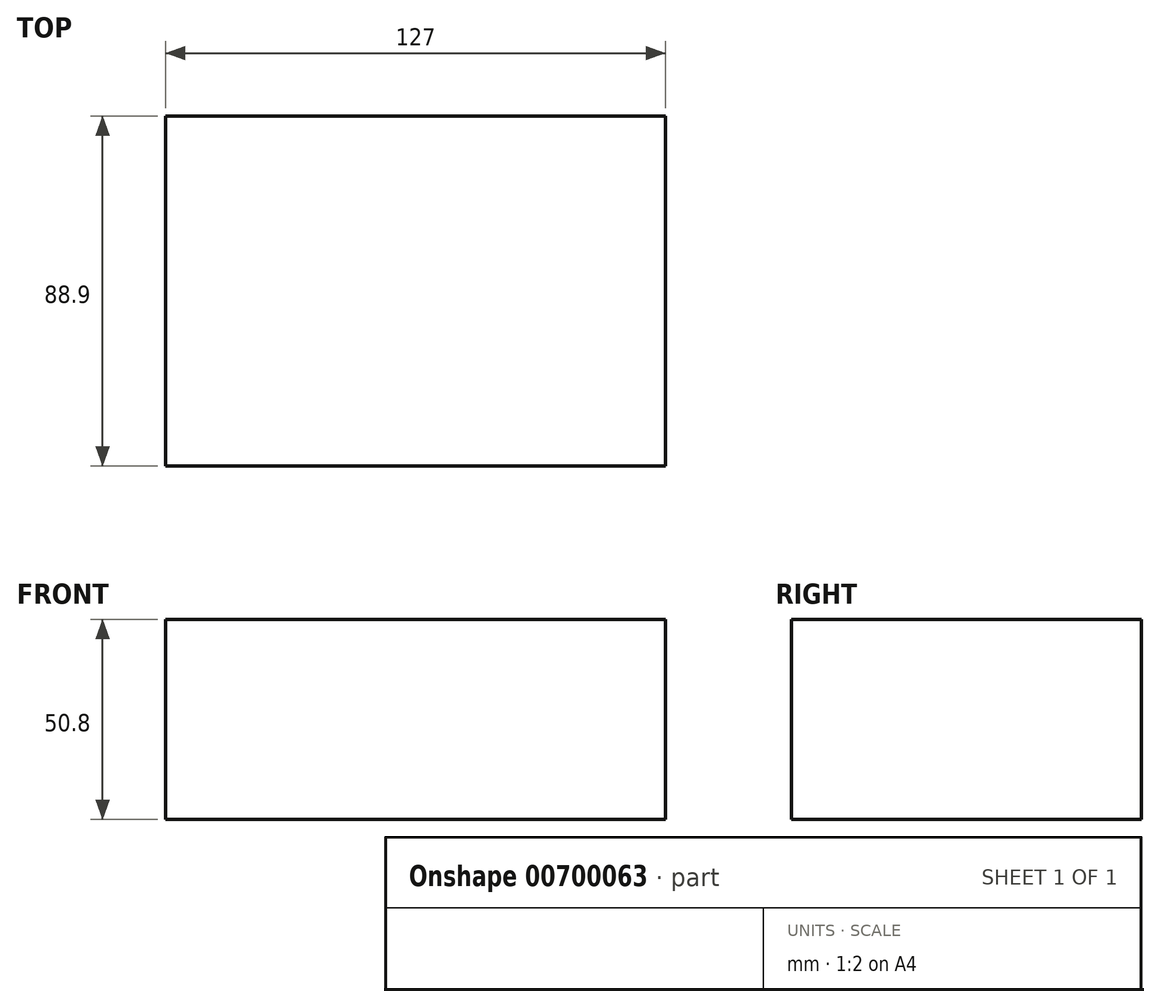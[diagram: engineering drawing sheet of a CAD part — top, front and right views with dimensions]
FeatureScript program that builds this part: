
annotation { "Feature Type Name" : "Feature", "Feature Type Description" : "" }
export const myFeature = defineFeature(function(context is Context, id is Id, definition is map)
    precondition{}
    {
        {
            var Q0;
            Q0=qCreatedBy(makeId("Front.planeOp"),FACE);
            var sketch = newSketch(context, id + "F0", { "sketchPlane" : qUnion([Q0])});
            skLineSegment(sketch, "E0.bottom", {"start": v(63.5, 25.4) * mm, "end": v(-63.5, 25.4) * mm});
            skLineSegment(sketch, "E0.top", {"start": v(63.5, -25.4) * mm, "end": v(-63.5, -25.4) * mm});
            skLineSegment(sketch, "E0.left", {"start": v(63.5, 25.4) * mm, "end": v(63.5, -25.4) * mm});
            skLineSegment(sketch, "E0.right", {"start": v(-63.5, 25.4) * mm, "end": v(-63.5, -25.4) * mm});
            skPoint(sketch, "E0.middle", {"position": v(0, 0) * mm});
            skSolve(sketch);
        }
        {
            var Q0;
            Q0 = qSketchRegion(id + "F0", true);
            extrude(context, id + "F1", {"entities" : qUnion([Q0]), "endBound" : BoundingType.SYMMETRIC, "depth" : 88.9 * mm, "offsetDistance" : 25.4 * mm});
        }
    });
